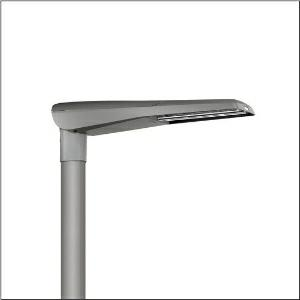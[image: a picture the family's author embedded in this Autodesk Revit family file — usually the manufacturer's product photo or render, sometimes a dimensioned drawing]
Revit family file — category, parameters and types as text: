
# Revit family: streetlight_sl_11_iq_mini___p1_0a_5xc2cc1f08ge_b649
name_source: partatom
category: Lighting Fixtures
units: mm (PartAtom-declared; Revit-internal decimal feet)

## family parameters
Cut with Voids When Loaded = No
Host = Face
Light Source = No
Part Type = Normal
Room Calculation Point = No
Round Connector Dimension = Use Diameter
Shared = No

## types (1)
- --- (1 x LED, 2590 lm, 21.6 W, 2200K)
    Apparent Load = 22 VA
    CIE Flux Codes = 28 62 91 100 100
    Color Rendering = 70
    Color Temperature = 2200K
    Default Elevation = 1800 mm
    Description = Streetlight SL 11 iQ mini, mast luminaire, primary light control with 3 zone facetted reflector, of plastic, silver coated, highly specular, primary optical cover: cover, of PMMA, transparent, light distribution: P1.0a, light emission: direct distribution, primary light characteristic: asymmetric, installation type: post-top, side-entry, lamps: LED, High Power LED, rated values: 3.030lm | 21,3W | 142,3lm/W (begin service life); end service life: 3.030lm | 21,9W; at 50% lumin. flux: 1.515lm | 11,2W | 135,3lm/W, colour temperature: 2200/2700/3000/4000K, colour rendering: CRI > 70, light colour: 722/727/730/740, light setting 1 begin service life: 100% | 3.030lm | 21,3W | 142,3lm/W | 3.000K, light setting 1 end service life: 21,9W, further light settings possible, control: Street-Remote, Auto-Match, Temp-Guard, Lumen-Switch, Night-Set, Smart-Wire, Light-Fading, Desk-Remote (wireless, voltage-free reading and setting of iQ features in the workshop via application-optimized NFC function/RFID function), optimised constant luminous flux control (CLO 2.0), with cable H07RN-F 3x 1.5mm², mains connection: 230..240V, AC, 50/60Hz, connection cable pre-assembled, cable length: 6,5m, luminaire housing, of diecast aluminium, powder-coated, SITECO metallic grey (DB 702S), please order mast flange separately, inclination adjustable without tools: 0°, 5°, 10°, 15° (post-top) | 0°, -5°, -10°, -15° (side-entry), sealing non-destructively replaceable, multi-level sealing system, length: 736mm, width: 174mm, height: 116mm, mast flange for spigot size: 42mm (side-entry): 5XC10008XM4, 60/48mm (side-entry/post-top): 5XC10108XM2, 76/60mm (side-entry/post-top): 5XC10108XM1, equipment: standard, protection rating (complete): IP66, insulation class (complete): insulation class II (safety insulation), certification: CE, ENEC, ENEC+, VDE, impact resistance: IK10, permissible operating ambient temperature for outdoor applications: -25..+50°C, standard-compliant lighting for roads and squares, Environmental Product Declaration (EPD) tested and certified by an independent institute, packaging unit: 1 piece

Light Distribution: P1.0a
    Height = 116 mm
    Lamp = 1 x LED
    Lamp Light Flux = 2590 lm
    Lamp Power = 21.6 W
    Lamp count = 1
    Length = 736 mm
    Luminous efficacy = 120 lm/W
    Manufacturer = Siteco
    ModVariant = No
    Model = 5XC2CC1F08GE
    Number of Poles = 1
    OnlyDefault = Yes
    Power Factor = 1
    Product Name = Streetlight SL 11 iQ mini | P1.0a
    Product group = mast luminaire | pylon top
    ProductGroupID = 6100
    Protection Class = Protection class II
    Protection Degree = IP 66
    RLX_Detail_Level = 1
    RLX_Emergency_Light_Flux = 0 lm
    RLX_Emergency_Type = 0
    RLX_Emergency_Type_DB = No
    RlxData = <blob elided: 53381 chars, md5=e696a947>
    Socket = socket
    Standby Power = 0 W
    System Light Flux = 2590 lm
    System Power = 22 W
    Type Comments = individual setting: luminous flux: 100 % | dim-lin: 254 | 299 mA
    Type Image = l_1003508.jpg
    URL = http://relux.com
    VarID = @adj_044407
    Voltage = 0 V
    Weight = 0.00 kg
    Width = 174 mm

## geometry (parser evidence)
native form markers: Blend x4, Sweep x10
no freeform markers — native parametric forms only
